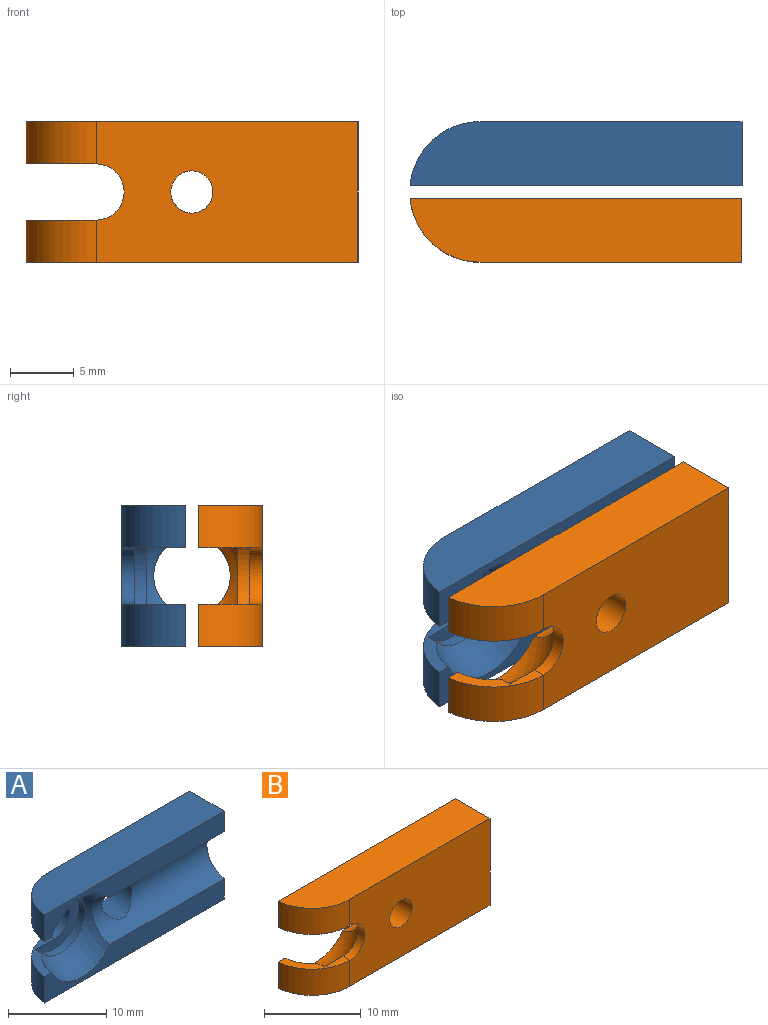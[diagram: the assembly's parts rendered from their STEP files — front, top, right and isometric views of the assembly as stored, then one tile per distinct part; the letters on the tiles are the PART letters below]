
ASSEMBLY  parts=2 mates=2
PART A: 16 faces, bbox 26x5.3x11 mm
  f0: cylinder r=2.2mm len=4.4mm, axis (0,-1,0), area 6.9mm2, adj f6,f7,f10,f15
  f1: cylinder r=3mm len=16.5mm, axis (1,0,0), area 123.2mm2, adj f8,f9,f11,f12,f13
  f2: cylinder r=5.5mm len=5.48mm, axis (0,0,-1), area 26.9mm2, adj f4,f7,f10,f12
  f3: cylinder r=5.5mm len=5.48mm, axis (0,0,1), area 26.9mm2, adj f5,f6,f10,f11
  f4: plane 25.98x5mm, normal (0,0,-1), area 123.5mm2, adj f2,f9,f10,f12
  f5: plane 25.98x5mm, normal (0,0,1), area 123.5mm2, adj f3,f9,f10,f11
  f6: plane 5.48x5mm, normal (0,0,-1), area 6.6mm2, adj f0,f3,f8,f11,f14,f15
  f7: plane 5.48x5mm, normal (0,0,1), area 6.6mm2, adj f0,f2,f8,f12,f14,f15
  f8: sphere r=5mm, area 67.9mm2, adj f1,f6,f7,f11,f12,f14
  f9: plane 11x5mm, normal (1,0,0), area 43.8mm2, adj f1,f4,f5,f10,f11,f12
  f10: plane 20.5x11mm, normal (0,1,0), area 203.4mm2, adj f0,f2,f3,f4,f5,f9,f13
  f11: plane 25.98x3.3mm, normal (0,-1,0), area 55.7mm2, adj f1,f3,f5,f6,f8,f9
  f12: plane 25.98x3.3mm, normal (0,-1,0), area 55.7mm2, adj f1,f2,f4,f7,f8,f9
  f13: cylinder r=2.15mm len=4.3mm, axis (0,1,0), area 39.6mm2, adj f1,f10
  f14: cylinder r=3.5mm len=7mm, axis (0,-1,0), area 16mm2, adj f6,f7,f8,f15
  f15: plane 7x6.22mm, normal (0,-1,0), area 16.6mm2, adj f0,f6,f7,f14
PART B: 16 faces, bbox 26x5.3x11 mm
  f0: cylinder r=3mm len=16.5mm, axis (1,0,0), area 130mm2, adj f3,f10,f11,f12,f13
  f1: plane 20.5x11mm, normal (0,-1,0), area 209.3mm2, adj f2,f6,f7,f8,f9,f10,f13
  f2: cylinder r=2.2mm len=4.4mm, axis (0,-1,0), area 6.9mm2, adj f1,f4,f5,f15
  f3: sphere r=5mm, area 67.9mm2, adj f0,f4,f5,f11,f12,f14
  f4: plane 5.48x5mm, normal (0,0,1), area 6.6mm2, adj f2,f3,f8,f12,f14,f15
  f5: plane 5.48x5mm, normal (0,0,-1), area 6.6mm2, adj f2,f3,f6,f11,f14,f15
  f6: cylinder r=5.5mm len=5.48mm, axis (0,0,1), area 26.9mm2, adj f1,f5,f9,f11
  f7: plane 25.98x5mm, normal (0,0,-1), area 123.5mm2, adj f1,f8,f10,f12
  f8: cylinder r=5.5mm len=5.48mm, axis (0,0,-1), area 26.9mm2, adj f1,f4,f7,f12
  f9: plane 25.98x5mm, normal (0,0,1), area 123.5mm2, adj f1,f6,f10,f11
  f10: plane 11x5mm, normal (1,0,0), area 43.8mm2, adj f0,f1,f7,f9,f11,f12
  f11: plane 25.98x3.3mm, normal (0,1,0), area 55.7mm2, adj f0,f3,f5,f6,f9,f10
  f12: plane 25.98x3.3mm, normal (0,1,0), area 55.7mm2, adj f0,f3,f4,f7,f8,f10
  f13: cylinder r=1.65mm len=3.3mm, axis (0,-1,0), area 28.4mm2, adj f0,f1
  f14: cylinder r=3.5mm len=7mm, axis (0,-1,0), area 16mm2, adj f3,f4,f5,f15
  f15: plane 7x6.22mm, normal (0,1,0), area 16.6mm2, adj f2,f4,f5,f14
PLACE A t=(25.68,-38.89,-24.54)mm fixed
PLACE B t=(25.68,-38.89,-24.54)mm
MATE revolute A.f13 <-> B.f13  axis (0,1,0) through (38.68,-33.39,5.46)mm
MATE parallel A.f5 <-> B.f9  axis (0,0,1) through (39.3,-35.96,10.96)mm
